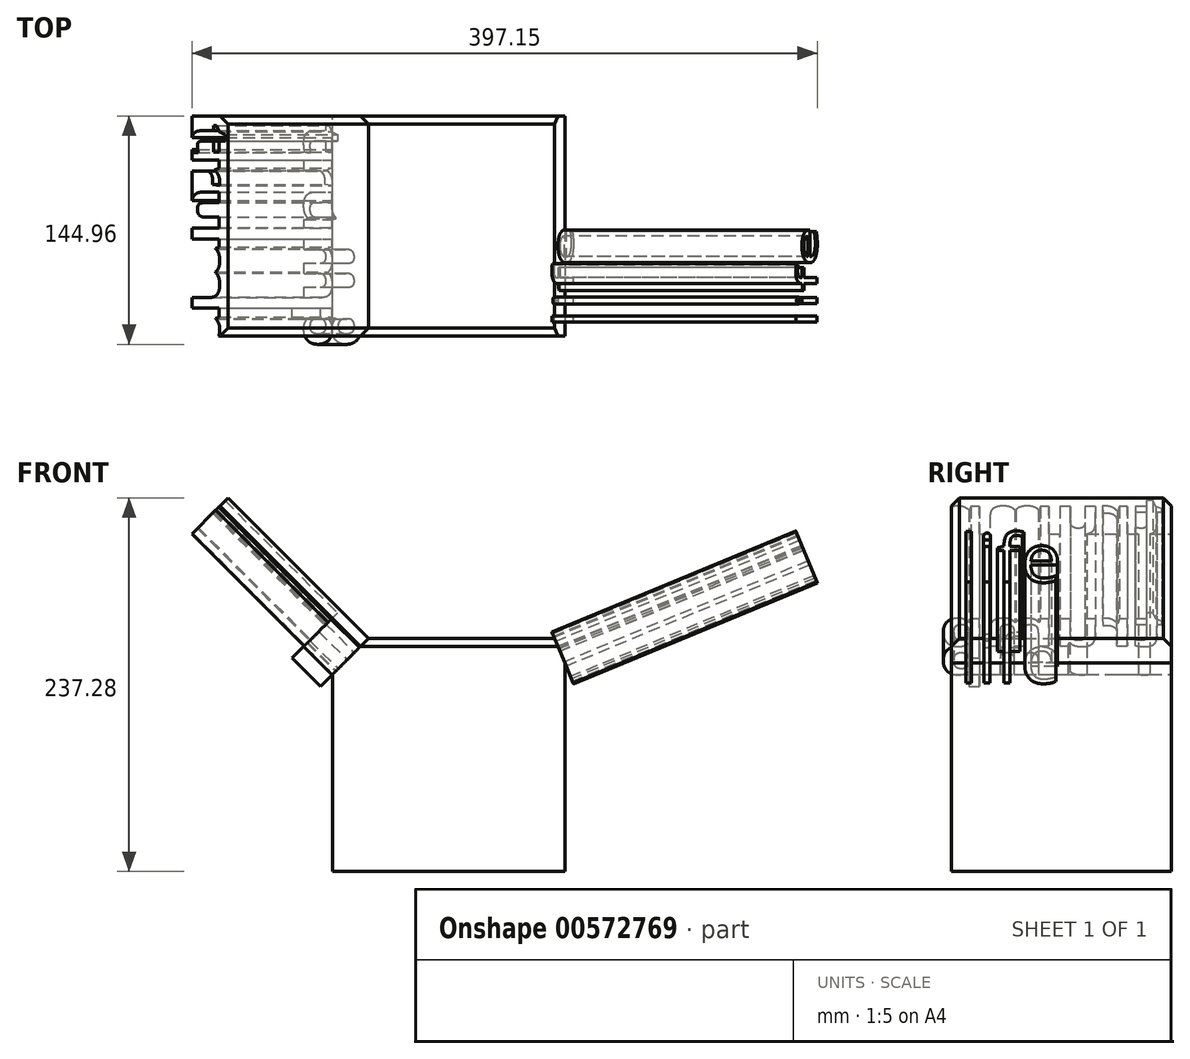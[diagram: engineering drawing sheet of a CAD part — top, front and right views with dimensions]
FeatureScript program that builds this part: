
annotation { "Feature Type Name" : "Feature", "Feature Type Description" : "" }
export const myFeature = defineFeature(function(context is Context, id is Id, definition is map)
    precondition{}
    {
        {
            var Q0;
            Q0=qCreatedBy(makeId("Front.planeOp"),FACE);
            var sketch = newSketch(context, id + "F0", { "sketchPlane" : qUnion([Q0])});
            skLineSegment(sketch, "E0.bottom", {"start": v(-75.06, 74.77) * mm, "end": v(72.45, 74.77) * mm});
            skLineSegment(sketch, "E0.top", {"start": v(-75.06, -73.24) * mm, "end": v(72.45, -73.24) * mm});
            skLineSegment(sketch, "E0.left", {"start": v(-75.06, 74.77) * mm, "end": v(-75.06, -73.24) * mm});
            skLineSegment(sketch, "E0.right", {"start": v(72.45, 74.77) * mm, "end": v(72.45, -73.24) * mm});
            skSolve(sketch);
        }
        {
            var Q0;
            Q0=makeQuery(id+"F0.imprint","IMPRINT",FACE,{"disambiguationData":[TD([[makeQuery(id+"F0.imprint","IMPRINT",EDGE,{"derivedFrom":sQuery(id+"F0.wireOp",EDGE,"E0.bottom")}),-1.0]])]});
            extrude(context, id + "F1", {"entities" : qUnion([Q0]), "depth" : 139.7 * mm, "offsetDistance" : 25.4 * mm});
        }
        {
            var Q0;
            Q0=makeQuery(id+"F1.opExtrude","SWEPT_EDGE",EDGE,{"disambiguationData":[OSD([sQuery(id+"F0.wireOp",EDGE,"E0.bottom"),sQuery(id+"F0.wireOp",EDGE,"E0.left")])]});
            chamfer(context, id + "F2", {"entities" : qUnion([Q0]), "width" : 22.86 * mm, "tangentPropagation" : true});
        }
        {
            var Q0;
            Q0=makeQuery(id+"F1.opExtrude","CAP_EDGE",EDGE,{"disambiguationData":[OSD([sQuery(id+"F0.wireOp",EDGE,"E0.bottom")])],"isStart":true});
            var Q1;
            Q1=makeQuery(id+"F1.opExtrude","SWEPT_EDGE",EDGE,{"disambiguationData":[OSD([sQuery(id+"F0.wireOp",EDGE,"E0.bottom"),sQuery(id+"F0.wireOp",EDGE,"E0.right")])]});
            var Q2;
            Q2=makeQuery(id+"F1.opExtrude","CAP_EDGE",EDGE,{"disambiguationData":[OSD([sQuery(id+"F0.wireOp",EDGE,"E0.bottom")])],"isStart":false});
            chamfer(context, id + "F3", {"entities" : qUnion([Q0, Q1, Q2]), "width" : 5.08 * mm, "tangentPropagation" : true});
        }
        {
            var Q0;
            Q0=makeQuery(id+"F2.opChamfer","BLEND_FACE",FACE,{"disambiguationData":[OSD([sQuery(id+"F0.wireOp",EDGE,"E0.bottom"),sQuery(id+"F0.wireOp",EDGE,"E0.left")])]});
            var sketch = newSketch(context, id + "F4", { "sketchPlane" : qUnion([Q0])});
            skText(sketch, "E1", { "text": "trump\n", "fontName": "OpenSans-Bold.ttf"});
            const initialGuessF4  = {"E1": [0.00508, -0.01637, 1, 0, 0.03233]};
            skSetInitialGuess(sketch, initialGuessF4);
            skSolve(sketch);
        }
        {
            var Q0;
            Q0 = qSketchRegion(id + "F4", true);
            extrude(context, id + "F5", {"entities" : qUnion([Q0]), "operationType" : NewBodyOperationType.ADD, "depth" : 25.4 * mm, "offsetDistance" : 25.4 * mm});
        }
        {
            var Q0;
            {var subQ0=sQuery(id+"F0.wireOp",EDGE,"E0.right");Q0=makeQuery(id+"F3.opChamfer","BLEND_EDGE",EDGE,{"blendedFrom":[makeQuery(id+"F1.opExtrude","SWEPT_EDGE",EDGE,{"disambiguationData":[OSD([sQuery(id+"F0.wireOp",EDGE,"E0.bottom"),subQ0])]}),makeQuery(id+"F1.opExtrude","SWEPT_FACE",FACE,{"disambiguationData":[OSD([subQ0])]})],"blendedInto":[makeQuery(id+"F1.opExtrude","SWEPT_FACE",FACE,{"disambiguationData":[OSD([subQ0])]})]});}
            chamfer(context, id + "F6", {"entities" : qUnion([Q0]), "width" : 25.4 * mm, "tangentPropagation" : true});
        }
        {
            var Q0;
            Q0=makeQuery(id+"F6.opChamfer","BLEND_FACE",FACE,{"disambiguationData":[OSD([sQuery(id+"F0.wireOp",EDGE,"E0.bottom"),sQuery(id+"F0.wireOp",EDGE,"E0.right")])]});
            var sketch = newSketch(context, id + "F7", { "sketchPlane" : qUnion([Q0])});
            skText(sketch, "E2", { "text": "life", "fontName": "OpenSans-Regular.ttf"});
            const initialGuessF7  = {"E2": [-0.13462, 0.01306, 1, 0, 0.03313]};
            skSetInitialGuess(sketch, initialGuessF7);
            skSolve(sketch);
        }
        {
            var Q0;
            Q0 = qSketchRegion(id + "F7", true);
            extrude(context, id + "F8", {"entities" : qUnion([Q0]), "operationType" : NewBodyOperationType.ADD, "depth" : 25.4 * mm, "offsetDistance" : 25.4 * mm});
        }
        {
            var Q0;
            Q0 = qSketchRegion(id + "F7", true);
            extrude(context, id + "F9", {"entities" : qUnion([Q0]), "operationType" : NewBodyOperationType.ADD, "depth" : 167.64 * mm, "offsetDistance" : 25.4 * mm});
        }
        {
            var Q0;
            {var subQ31=sQuery(id+"F0.wireOp",EDGE,"E0.bottom");var subQ32=sQuery(id+"F0.wireOp",EDGE,"E0.left");Q0=makeQuery(id+"F5.boolean.opBoolean","SPLIT",FACE,{"disambiguationData":[TD([makeQuery(id+"F1.opExtrude","SWEPT_FACE",FACE,{"disambiguationData":[OSD([subQ31])]})])],"derivedFrom":makeQuery(id+"F2.opChamfer","BLEND_FACE",FACE,{"disambiguationData":[OSD([subQ31,subQ32])]})});}
            extrude(context, id + "F10", {"entities" : qUnion([Q0]), "operationType" : NewBodyOperationType.ADD, "depth" : 126.24 * mm, "offsetDistance" : 25.4 * mm});
        }
    });
